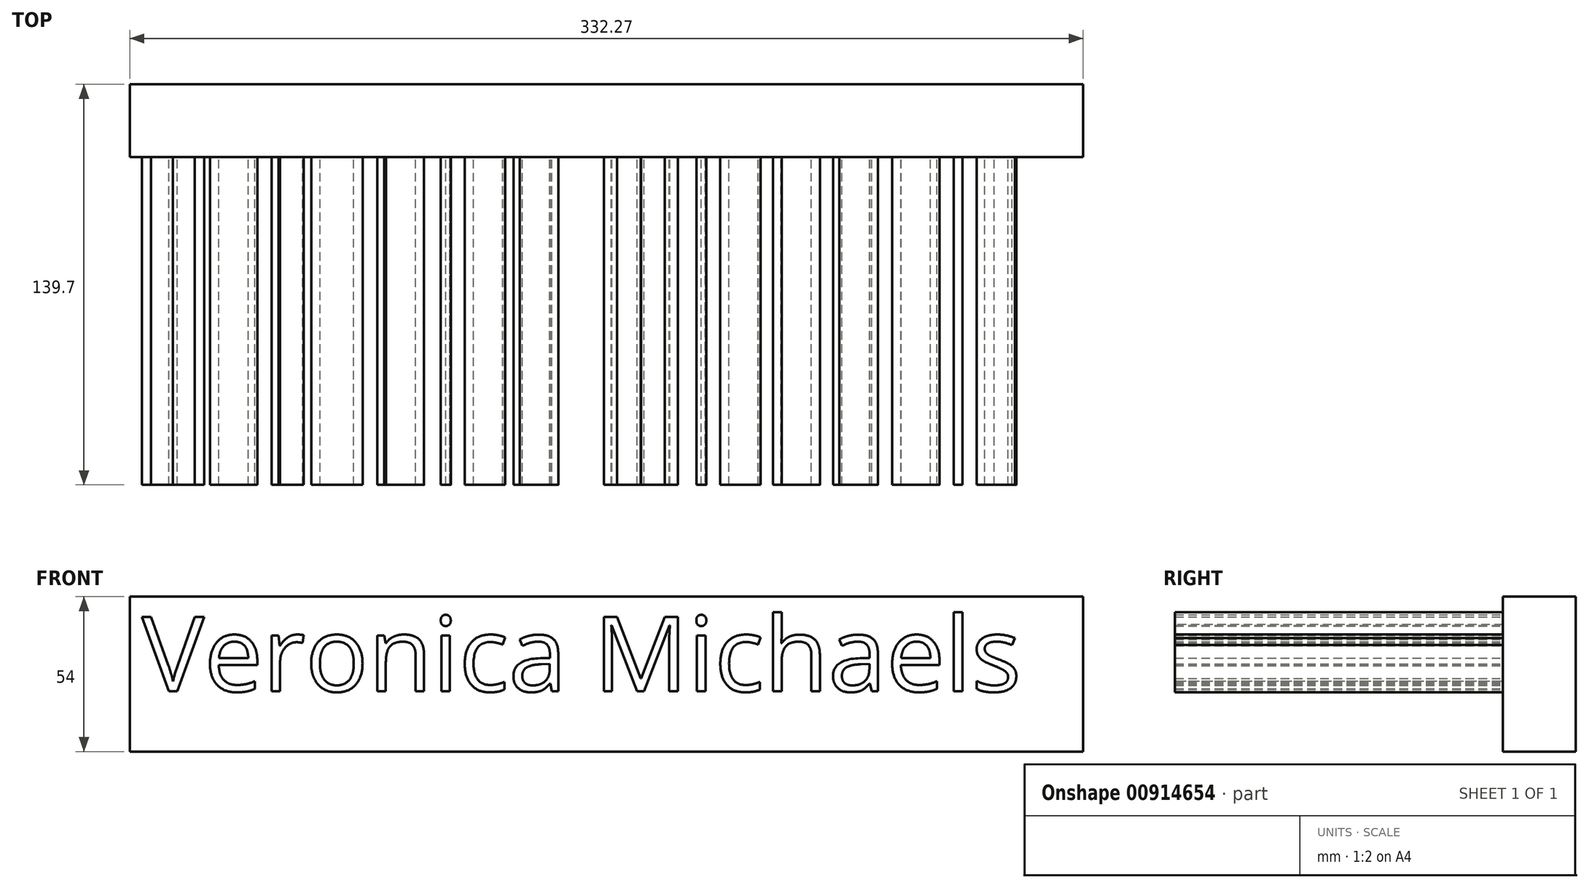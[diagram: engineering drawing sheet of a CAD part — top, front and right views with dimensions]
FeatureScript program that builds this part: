
annotation { "Feature Type Name" : "Feature", "Feature Type Description" : "" }
export const myFeature = defineFeature(function(context is Context, id is Id, definition is map)
    precondition{}
    {
        {
            var Q0;
            Q0=qCreatedBy(makeId("Front.planeOp"),FACE);
            var sketch = newSketch(context, id + "F0", { "sketchPlane" : qUnion([Q0])});
            skLineSegment(sketch, "E0.bottom", {"start": v(-78.4, 54) * mm, "end": v(253.86, 54) * mm});
            skLineSegment(sketch, "E0.top", {"start": v(-78.4, 0) * mm, "end": v(253.86, 0) * mm});
            skLineSegment(sketch, "E0.left", {"start": v(-78.4, 54) * mm, "end": v(-78.4, 0) * mm});
            skLineSegment(sketch, "E0.right", {"start": v(253.86, 54) * mm, "end": v(253.86, 0) * mm});
            skSolve(sketch);
        }
        {
            var Q0;
            Q0=makeQuery(id+"F0.imprint","IMPRINT",FACE,{"disambiguationData":[TD([[makeQuery(id+"F0.imprint","IMPRINT",EDGE,{"derivedFrom":sQuery(id+"F0.wireOp",EDGE,"E0.bottom")}),-1.0]])]});
            extrude(context, id + "F1", {"entities" : qUnion([Q0]), "depth" : 25.4 * mm, "offsetDistance" : 25.4 * mm});
        }
        {
            var Q0;
            Q0=makeQuery(id+"F1.opExtrude","CAP_FACE",FACE,{"disambiguationData":[OSD([sQuery(id+"F0.wireOp",EDGE,"E0.bottom"),sQuery(id+"F0.wireOp",EDGE,"E0.top"),sQuery(id+"F0.wireOp",EDGE,"E0.left"),sQuery(id+"F0.wireOp",EDGE,"E0.right")])],"isStart":false});
            var sketch = newSketch(context, id + "F2", { "sketchPlane" : qUnion([Q0])});
            skText(sketch, "E1", { "text": "Veronica Michaels \n", "fontName": "OpenSans-Regular.ttf"});
            const initialGuessF2  = {"E1": [-0.0742, 0.02098, 1, 0, 0.0262]};
            skSetInitialGuess(sketch, initialGuessF2);
            skSolve(sketch);
        }
        {
            var Q0;
            Q0 = qSketchRegion(id + "F2", true);
            extrude(context, id + "F3", {"entities" : qUnion([Q0]), "operationType" : NewBodyOperationType.ADD, "depth" : 114.3 * mm, "offsetDistance" : 25.4 * mm});
        }
    });
